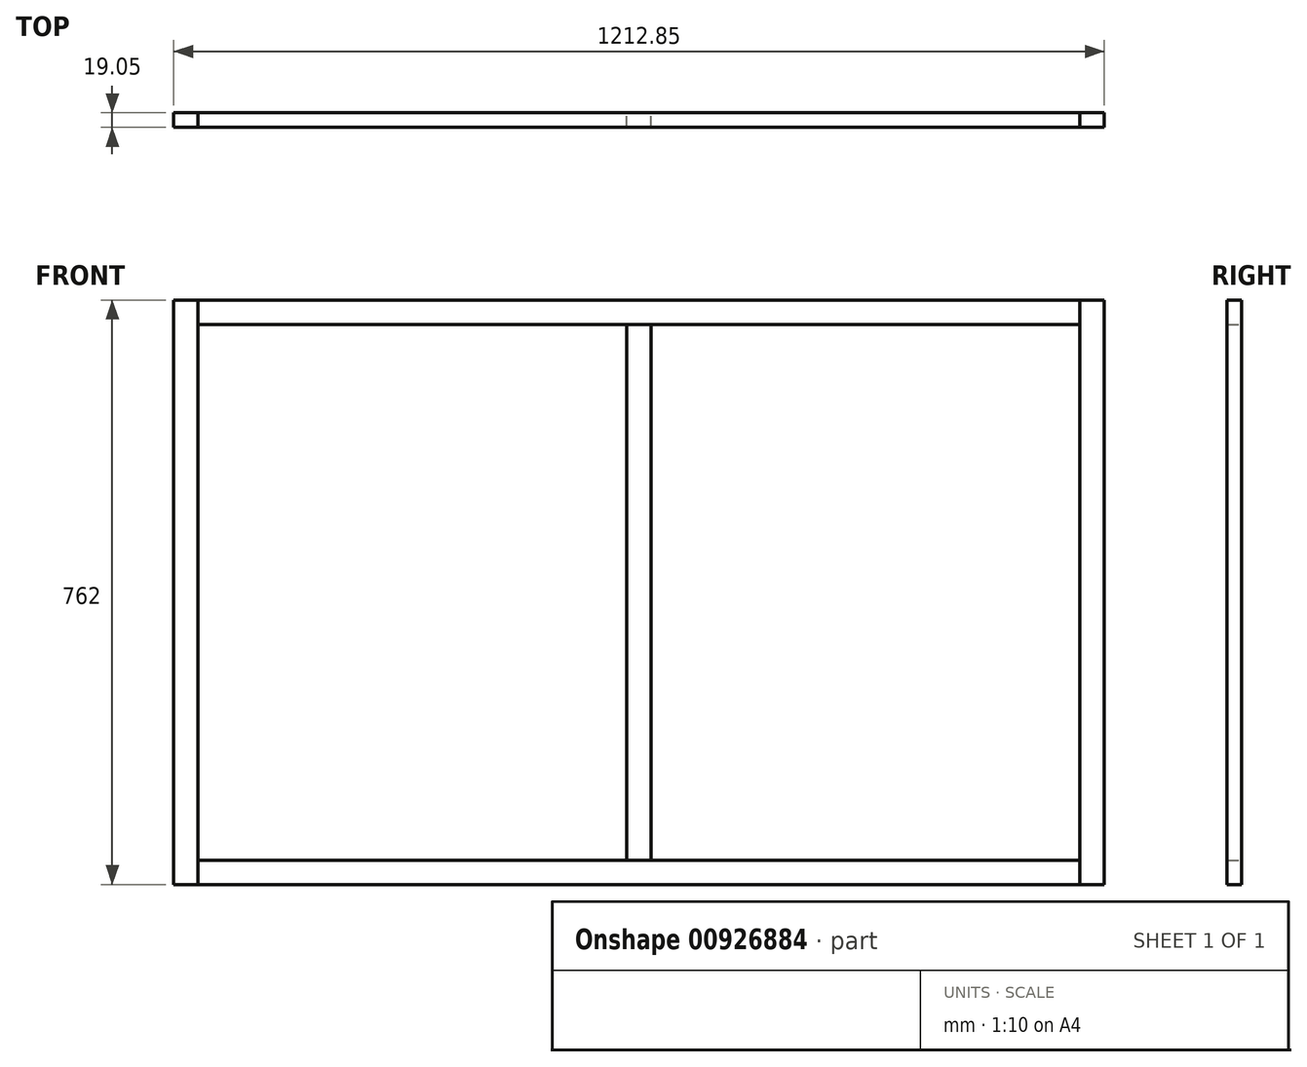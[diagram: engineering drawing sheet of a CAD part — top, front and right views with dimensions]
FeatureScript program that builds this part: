
annotation { "Feature Type Name" : "Feature", "Feature Type Description" : "" }
export const myFeature = defineFeature(function(context is Context, id is Id, definition is map)
    precondition{}
    {
        {
            var Q0;
            Q0=qCreatedBy(makeId("Front.planeOp"),FACE);
            var sketch = newSketch(context, id + "F0", { "sketchPlane" : qUnion([Q0])});
            skLineSegment(sketch, "E0.bottom", {"start": v(-504.15, -425.83) * mm, "end": v(708.7, -425.83) * mm});
            skLineSegment(sketch, "E0.top", {"start": v(-504.15, 336.17) * mm, "end": v(708.7, 336.17) * mm});
            skLineSegment(sketch, "E0.left", {"start": v(-504.15, -425.83) * mm, "end": v(-504.15, 336.17) * mm});
            skLineSegment(sketch, "E0.right", {"start": v(708.7, -425.83) * mm, "end": v(708.7, 336.17) * mm});
            skLineSegment(sketch, "E1.0", {"start": v(-472.4, -394.08) * mm, "end": v(-472.4, 304.42) * mm});
            skLineSegment(sketch, "E1.1", {"start": v(-472.4, -394.08) * mm, "end": v(676.95, -394.08) * mm});
            skLineSegment(sketch, "E1.2", {"start": v(676.95, -394.08) * mm, "end": v(676.95, 304.42) * mm});
            skLineSegment(sketch, "E1.3", {"start": v(-472.4, 304.42) * mm, "end": v(676.95, 304.42) * mm});
            skLineSegment(sketch, "E2.bottom", {"start": v(-472.4, 177.3) * mm, "end": v(676.95, 177.3) * mm});
            skLineSegment(sketch, "E2.top", {"start": v(-472.4, 145.56) * mm, "end": v(676.95, 145.56) * mm});
            skLineSegment(sketch, "E2.left", {"start": v(-472.4, 177.3) * mm, "end": v(-472.4, 145.56) * mm});
            skLineSegment(sketch, "E2.right", {"start": v(676.95, 177.3) * mm, "end": v(676.95, 145.56) * mm});
            skLineSegment(sketch, "E3.bottom", {"start": v(-472.4, -95.63) * mm, "end": v(676.95, -95.63) * mm});
            skLineSegment(sketch, "E3.top", {"start": v(-472.4, -127.38) * mm, "end": v(676.95, -127.38) * mm});
            skLineSegment(sketch, "E3.left", {"start": v(-472.4, -95.63) * mm, "end": v(-472.4, -127.38) * mm});
            skLineSegment(sketch, "E3.right", {"start": v(676.95, -95.63) * mm, "end": v(676.95, -127.38) * mm});
            skPoint(sketch, "E4", {"position": v(-472.4, -111.5) * mm});
            skLineSegment(sketch, "E5", {"start": v(-478.75, -140.08) * mm, "end": v(-478.75, -143.25) * mm, "construction": true});
            skPoint(sketch, "E6", {"position": v(-478.75, -141.66) * mm});
            skLineSegment(sketch, "E7", {"start": v(-478.75, 120.27) * mm, "end": v(-478.75, 117.1) * mm, "construction": true});
            skPoint(sketch, "E8", {"position": v(-478.75, 118.69) * mm});
            skPoint(sketch, "E9", {"position": v(-472.4, 161.43) * mm});
            skLineSegment(sketch, "E10", {"start": v(-472.4, 304.42) * mm, "end": v(-472.4, 336.17) * mm});
            skLineSegment(sketch, "E11", {"start": v(676.95, 304.42) * mm, "end": v(676.95, 336.17) * mm});
            skLineSegment(sketch, "E12", {"start": v(-472.4, -394.08) * mm, "end": v(-472.4, -425.83) * mm});
            skLineSegment(sketch, "E13", {"start": v(676.95, -394.08) * mm, "end": v(676.95, -425.83) * mm});
            skLineSegment(sketch, "E14", {"start": v(-509.68, 163.02) * mm, "end": v(-509.68, 159.84) * mm, "construction": true});
            skPoint(sketch, "E15", {"position": v(-509.68, 161.43) * mm});
            skLineSegment(sketch, "E16", {"start": v(102.28, 304.42) * mm, "end": v(102.28, -394.08) * mm, "construction": true});
            skLineSegment(sketch, "E17.0", {"start": v(86.4, 304.42) * mm, "end": v(86.4, -394.08) * mm});
            skLineSegment(sketch, "E18.MirrorCS", {"start": v(118.15, 304.42) * mm, "end": v(118.15, -394.08) * mm});
            skSolve(sketch);
        }
        {
            var Q0;
            {var subQ0=sQuery(id+"F0.wireOp",EDGE,"E0.left");Q0=makeQuery(id+"F0.imprint","IMPRINT",FACE,{"disambiguationData":[TD([[makeQuery(id+"F0.imprint","IMPRINT",EDGE,{"derivedFrom":subQ0}),-1.0]])]});}
            var Q1;
            {var subQ0=sQuery(id+"F0.wireOp",EDGE,"E17.0");var subQ1=sQuery(id+"F0.wireOp",EDGE,"E2.top");var subQ2=makeQuery(id+"F0.imprint","INTERSECT",VERTEX,{"derivedFrom":[subQ1,subQ0]});Q1=makeQuery(id+"F0.imprint","IMPRINT",FACE,{"disambiguationData":[TD([[makeQuery(id+"F0.imprint","IMPRINT",EDGE,{"disambiguationData":[TD([[subQ2,-1.0]])],"derivedFrom":subQ1}),-1.0]])]});}
            var Q2;
            {var subQ0=sQuery(id+"F0.wireOp",EDGE,"E17.0");var subQ1=sQuery(id+"F0.wireOp",EDGE,"E2.bottom");var subQ2=makeQuery(id+"F0.imprint","INTERSECT",VERTEX,{"derivedFrom":[subQ1,subQ0]});Q2=makeQuery(id+"F0.imprint","IMPRINT",FACE,{"disambiguationData":[TD([[makeQuery(id+"F0.imprint","IMPRINT",EDGE,{"disambiguationData":[TD([[subQ2,-1.0]])],"derivedFrom":subQ1}),-1.0]])]});}
            var Q3;
            {var subQ0=sQuery(id+"F0.wireOp",EDGE,"E17.0");var subQ1=sQuery(id+"F0.wireOp",EDGE,"E1.3");var subQ2=makeQuery(id+"F0.imprint","INTERSECT",VERTEX,{"derivedFrom":[subQ1,subQ0]});Q3=makeQuery(id+"F0.imprint","IMPRINT",FACE,{"disambiguationData":[TD([[makeQuery(id+"F0.imprint","IMPRINT",EDGE,{"disambiguationData":[TD([[subQ2,-1.0]])],"derivedFrom":subQ1}),-1.0]])]});}
            var Q4;
            {var subQ0=sQuery(id+"F0.wireOp",EDGE,"E17.0");var subQ1=sQuery(id+"F0.wireOp",EDGE,"E1.1");var subQ2=makeQuery(id+"F0.imprint","INTERSECT",VERTEX,{"derivedFrom":[subQ1,subQ0]});Q4=makeQuery(id+"F0.imprint","IMPRINT",FACE,{"disambiguationData":[TD([[makeQuery(id+"F0.imprint","IMPRINT",EDGE,{"disambiguationData":[TD([[subQ2,-1.0]])],"derivedFrom":subQ1}),1.0]])]});}
            var Q5;
            {var subQ0=sQuery(id+"F0.wireOp",EDGE,"E17.0");var subQ1=sQuery(id+"F0.wireOp",EDGE,"E3.bottom");var subQ2=makeQuery(id+"F0.imprint","INTERSECT",VERTEX,{"derivedFrom":[subQ1,subQ0]});Q5=makeQuery(id+"F0.imprint","IMPRINT",FACE,{"disambiguationData":[TD([[makeQuery(id+"F0.imprint","IMPRINT",EDGE,{"disambiguationData":[TD([[subQ2,-1.0]])],"derivedFrom":subQ1}),-1.0]])]});}
            var Q6;
            {var subQ3=sQuery(id+"F0.wireOp",EDGE,"E0.right");Q6=makeQuery(id+"F0.imprint","IMPRINT",FACE,{"disambiguationData":[TD([[makeQuery(id+"F0.imprint","IMPRINT",EDGE,{"derivedFrom":subQ3}),1.0]])]});}
            extrude(context, id + "F1", {"entities" : qUnion([Q0, Q1, Q2, Q3, Q4, Q5, Q6]), "depth" : 19.05 * mm, "offsetDistance" : 25.4 * mm});
        }
        {
            var Q0;
            {var subQ3=sQuery(id+"F0.wireOp",EDGE,"E10");Q0=makeQuery(id+"F0.imprint","IMPRINT",FACE,{"disambiguationData":[TD([[makeQuery(id+"F0.imprint","IMPRINT",EDGE,{"derivedFrom":subQ3}),-1.0]])]});}
            var Q1;
            {var subQ0=sQuery(id+"F0.wireOp",EDGE,"E2.left");Q1=makeQuery(id+"F0.imprint","IMPRINT",FACE,{"disambiguationData":[TD([[makeQuery(id+"F0.imprint","IMPRINT",EDGE,{"derivedFrom":subQ0}),1.0]])]});}
            var Q2;
            {var subQ0=sQuery(id+"F0.wireOp",EDGE,"E3.left");Q2=makeQuery(id+"F0.imprint","IMPRINT",FACE,{"disambiguationData":[TD([[makeQuery(id+"F0.imprint","IMPRINT",EDGE,{"derivedFrom":subQ0}),1.0]])]});}
            var Q3;
            {var subQ4=sQuery(id+"F0.wireOp",EDGE,"E12");Q3=makeQuery(id+"F0.imprint","IMPRINT",FACE,{"disambiguationData":[TD([[makeQuery(id+"F0.imprint","IMPRINT",EDGE,{"derivedFrom":subQ4}),1.0]])]});}
            var Q4;
            {var subQ0=sQuery(id+"F0.wireOp",EDGE,"E3.right");Q4=makeQuery(id+"F0.imprint","IMPRINT",FACE,{"disambiguationData":[TD([[makeQuery(id+"F0.imprint","IMPRINT",EDGE,{"derivedFrom":subQ0}),-1.0]])]});}
            var Q5;
            {var subQ0=sQuery(id+"F0.wireOp",EDGE,"E2.right");Q5=makeQuery(id+"F0.imprint","IMPRINT",FACE,{"disambiguationData":[TD([[makeQuery(id+"F0.imprint","IMPRINT",EDGE,{"derivedFrom":subQ0}),-1.0]])]});}
            extrude(context, id + "F2", {"entities" : qUnion([Q0, Q1, Q2, Q3, Q4, Q5]), "depth" : 19.05 * mm, "offsetDistance" : 25.4 * mm});
        }
    });
